# Revit family: Worksurfaces-Teknion-JNWPGN_Writable_Glass_Peninsula_Worksurface_Connected-R2018
name_source: partatom
category: Furniture
revit_build: Autodesk Revit 2018 (Build: 20190510_1515(x64)
units: mm (PartAtom-declared; Revit-internal decimal feet)

## family parameters
Always vertical = Yes
Cut with Voids When Loaded = No
OmniClass Number = 23.40.20.00
OmniClass Title = General Furniture and Specialties
Room Calculation Point = No
Shared = Yes
Work Plane-Based = No

## types (3) — shared parameters
Assembly Code = E2020200
Companion Finish = Paint - Teknion - Accent - Mineral Teal
Manufacturer = Teknion
Manufacturer Fax = 416.661.4586
Metal Edge Finish = Paint - Teknion - Mica - Anthracite
Part Number = JNWPGN
Product Documentation Link = https://www.teknion.com
Product Line = Expansion Cityline
Product Page URL = https://www.teknion.com
Series = Expansion Cityline
Sustainability Data = https://www.teknion.com
URL = www.teknion.com
Unit Weight URL = http://www.teknion.com
Warranty = http://www.teknion.com
Worksurface Finish = Back-painted Glass - K7 - Teknion - Very White

## per-type parameters (varying)
| type | Depth | Description | Model |
| 36" Depth | 36 " | Writable Glass Peninsula Worksurface – Worksurface Connected, 36" Depth, With Companion Marker Kit | JNWPGN36___K |
| 24" Depth | 24 " | Writable Glass Peninsula Worksurface – Worksurface Connected, 24" Depth, With Companion Marker Kit | JNWPGN24___K |
| 30" Depth | 30 " | Writable Glass Peninsula Worksurface – Worksurface Connected, 30" Depth, With Companion Marker Kit | JNWPGN30___K |

## geometry (parser evidence)
native form markers: Sweep x2
no freeform markers — native parametric forms only
